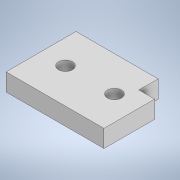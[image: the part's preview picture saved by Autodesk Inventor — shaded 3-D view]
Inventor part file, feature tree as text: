
AUTODESK INVENTOR PART (.ipt)
format: ipt  version: 2022 (Build 260153000, 153)  size: 113,664 bytes
history: native  units: in
note: dims shown in document units (in); Inventor stores cm internally (conversion verified against a paired STEP export)
features: sketch x4, extrude x3
ambient origin geometry x8: Origin, YZ Plane, XZ Plane, XY Plane, X Axis, Y Axis, Z Axis, Center Point
bodies: Solid1 (feature_tree)
feature tree (7):
  sketch  "Sketch1"  dims[d0=1.1024in d1=0.7874in]
  extrude  "Extrusion1"  Depth=0.7874in
  extrude  "Extrusion2"  Depth=0.1969in
  extrude  "Extrusion3"  Depth=0.2362in TaperAngle=0.0deg
  sketch  "Sketch2"  dims[d2=0.1969in d3=0.0in d4=0.1575in]
  sketch  "Sketch3"  dims[d5=0.1575in d6=0.2362in d7=0.0in]
  sketch  "Sketch4"  dims[d8=0.2362in d9=0.0in]
